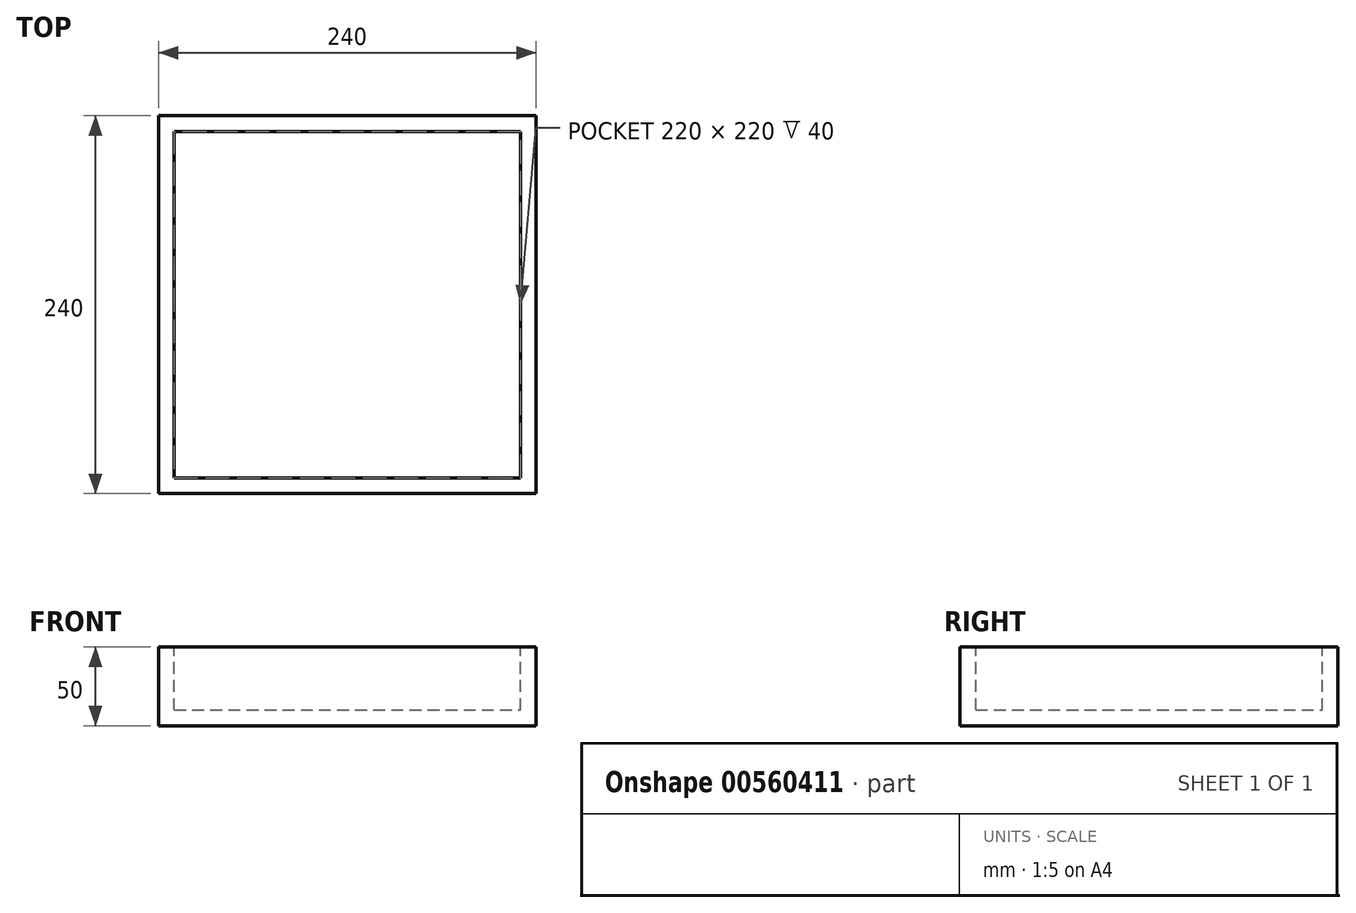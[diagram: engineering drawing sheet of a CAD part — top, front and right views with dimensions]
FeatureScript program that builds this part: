
annotation { "Feature Type Name" : "Feature", "Feature Type Description" : "" }
export const myFeature = defineFeature(function(context is Context, id is Id, definition is map)
    precondition{}
    {
        {
            var Q0;
            Q0=qCreatedBy(makeId("Top.planeOp"),FACE);
            var sketch = newSketch(context, id + "F0", { "sketchPlane" : qUnion([Q0])});
            skLineSegment(sketch, "E0.bottom", {"start": v(-120, 120) * mm, "end": v(120, 120) * mm});
            skLineSegment(sketch, "E0.top", {"start": v(-120, -120) * mm, "end": v(120, -120) * mm});
            skLineSegment(sketch, "E0.left", {"start": v(-120, 120) * mm, "end": v(-120, -120) * mm});
            skLineSegment(sketch, "E0.right", {"start": v(120, 120) * mm, "end": v(120, -120) * mm});
            skLineSegment(sketch, "E1", {"start": v(-120, 120) * mm, "end": v(120, -120) * mm, "construction": true});
            skLineSegment(sketch, "E2", {"start": v(-120, -120) * mm, "end": v(120, 120) * mm, "construction": true});
            skSolve(sketch);
        }
        {
            var Q0;
            Q0 = qSketchRegion(id + "F0", true);
            extrude(context, id + "F1", {"entities" : qUnion([Q0]), "depth" : 50 * mm, "offsetDistance" : 25 * mm});
        }
        {
            var Q0;
            Q0=makeQuery(id+"F1.opExtrude","CAP_FACE",FACE,{"disambiguationData":[OSD([sQuery(id+"F0.wireOp",EDGE,"E0.bottom"),sQuery(id+"F0.wireOp",EDGE,"E0.top"),sQuery(id+"F0.wireOp",EDGE,"E0.left"),sQuery(id+"F0.wireOp",EDGE,"E0.right")])],"isStart":false});
            var sketch = newSketch(context, id + "F2", { "sketchPlane" : qUnion([Q0])});
            skLineSegment(sketch, "E3.bottom", {"start": v(-110, -110) * mm, "end": v(110, -110) * mm});
            skLineSegment(sketch, "E3.top", {"start": v(-110, 110) * mm, "end": v(110, 110) * mm});
            skLineSegment(sketch, "E3.left", {"start": v(-110, -110) * mm, "end": v(-110, 110) * mm});
            skLineSegment(sketch, "E3.right", {"start": v(110, -110) * mm, "end": v(110, 110) * mm});
            skLineSegment(sketch, "E4", {"start": v(-110, -110) * mm, "end": v(110, 110) * mm, "construction": true});
            skLineSegment(sketch, "E5", {"start": v(110, -110) * mm, "end": v(-110, 110) * mm, "construction": true});
            skSolve(sketch);
        }
        {
            var Q0;
            Q0 = qSketchRegion(id + "F2", true);
            extrude(context, id + "F3", {"entities" : qUnion([Q0]), "operationType" : NewBodyOperationType.REMOVE, "oppositeDirection" : true, "depth" : 40 * mm, "offsetDistance" : 25 * mm});
        }
    });
